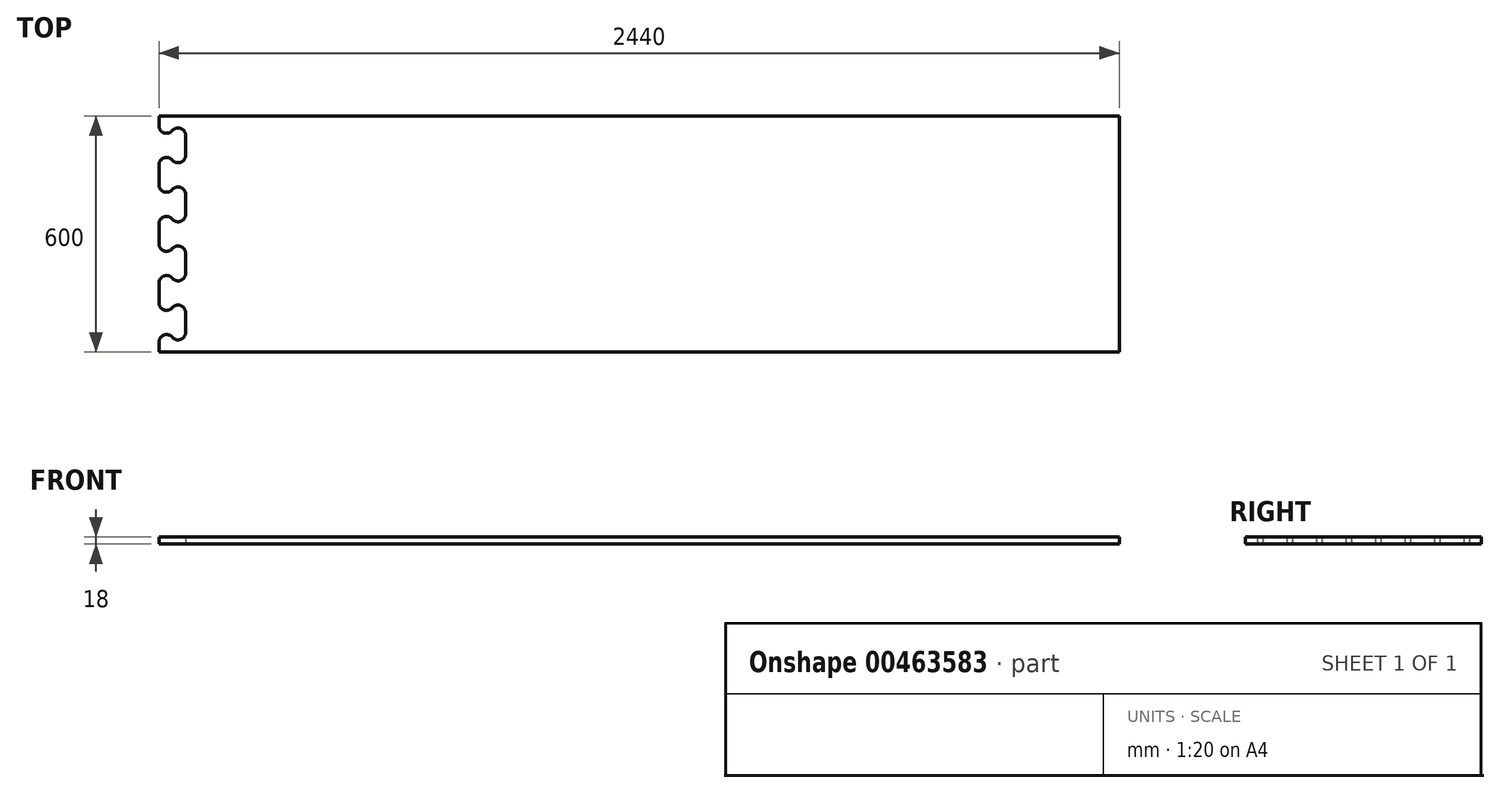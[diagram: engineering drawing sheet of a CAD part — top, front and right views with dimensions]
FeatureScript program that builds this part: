
annotation { "Feature Type Name" : "Feature", "Feature Type Description" : "" }
export const myFeature = defineFeature(function(context is Context, id is Id, definition is map)
    precondition{}
    {
        {
            var Q0;
            Q0=qCreatedBy(makeId("Top.planeOp"),FACE);
            var sketch = newSketch(context, id + "F0", { "sketchPlane" : qUnion([Q0])});
            skLineSegment(sketch, "E0.bottom", {"start": v(-1236.35, 978.6) * mm, "end": v(1203.65, 978.6) * mm});
            skLineSegment(sketch, "E0.right", {"start": v(1203.65, 978.6) * mm, "end": v(1203.65, 378.6) * mm});
            skLineSegment(sketch, "E1", {"start": v(-1236.35, 978.6) * mm, "end": v(-1236.35, 953.6) * mm});
            skLineSegment(sketch, "E2", {"start": v(-1236.35, 953.6) * mm, "end": v(-1236.35, 903.6) * mm, "construction": true});
            skLineSegment(sketch, "E3", {"start": v(-1168.41, 928.6) * mm, "end": v(-1168.41, 903.6) * mm});
            skLineSegment(sketch, "E4", {"start": v(-1236.35, 903.6) * mm, "end": v(-1168.41, 903.6) * mm, "construction": true});
            skLineSegment(sketch, "E5", {"start": v(-1236.35, 953.6) * mm, "end": v(-1168.41, 928.6) * mm, "construction": true});
            skArc(sketch, "E6", {"start": v(-1236.35, 953.6) * mm, "mid": v(-1223.73, 935.5) * mm, "end": v(-1202.38, 941.1) * mm});
            skArc(sketch, "E7", {"start": v(-1168.41, 928.6) * mm, "mid": v(-1181.04, 946.7) * mm, "end": v(-1202.38, 941.1) * mm});
            skArc(sketch, "E8.MirrorCS", {"start": v(-1236.35, 853.6) * mm, "mid": v(-1223.73, 871.7) * mm, "end": v(-1202.38, 866.1) * mm});
            skArc(sketch, "E9.MirrorCS", {"start": v(-1168.41, 878.6) * mm, "mid": v(-1181.04, 860.5) * mm, "end": v(-1202.38, 866.1) * mm});
            skLineSegment(sketch, "E10.MirrorCS", {"start": v(-1168.41, 878.6) * mm, "end": v(-1168.41, 903.6) * mm});
            skLineSegment(sketch, "E11", {"start": v(-1236.35, 853.6) * mm, "end": v(-1236.35, 803.6) * mm});
            skArc(sketch, "E12.0.1.0", {"start": v(-1236.35, 803.6) * mm, "mid": v(-1223.73, 785.5) * mm, "end": v(-1202.38, 791.1) * mm});
            skArc(sketch, "E12.0.1.1", {"start": v(-1168.41, 778.6) * mm, "mid": v(-1181.04, 796.7) * mm, "end": v(-1202.38, 791.1) * mm});
            skLineSegment(sketch, "E12.0.1.2", {"start": v(-1168.41, 778.6) * mm, "end": v(-1168.41, 753.6) * mm});
            skLineSegment(sketch, "E12.0.1.3", {"start": v(-1168.41, 728.6) * mm, "end": v(-1168.41, 753.6) * mm});
            skArc(sketch, "E12.0.1.4", {"start": v(-1168.41, 728.6) * mm, "mid": v(-1181.04, 710.5) * mm, "end": v(-1202.38, 716.1) * mm});
            skArc(sketch, "E12.0.1.5", {"start": v(-1236.35, 703.6) * mm, "mid": v(-1223.73, 721.7) * mm, "end": v(-1202.38, 716.1) * mm});
            skLineSegment(sketch, "E12.0.1.6", {"start": v(-1236.35, 703.6) * mm, "end": v(-1236.35, 653.6) * mm});
            skArc(sketch, "E12.0.2.0", {"start": v(-1236.35, 653.6) * mm, "mid": v(-1223.73, 635.5) * mm, "end": v(-1202.38, 641.1) * mm});
            skArc(sketch, "E12.0.2.1", {"start": v(-1168.41, 628.6) * mm, "mid": v(-1181.04, 646.7) * mm, "end": v(-1202.38, 641.1) * mm});
            skLineSegment(sketch, "E12.0.2.2", {"start": v(-1168.41, 628.6) * mm, "end": v(-1168.41, 603.6) * mm});
            skLineSegment(sketch, "E12.0.2.3", {"start": v(-1168.41, 578.6) * mm, "end": v(-1168.41, 603.6) * mm});
            skArc(sketch, "E12.0.2.4", {"start": v(-1168.41, 578.6) * mm, "mid": v(-1181.04, 560.5) * mm, "end": v(-1202.38, 566.1) * mm});
            skArc(sketch, "E12.0.2.5", {"start": v(-1236.35, 553.6) * mm, "mid": v(-1223.73, 571.7) * mm, "end": v(-1202.38, 566.1) * mm});
            skLineSegment(sketch, "E12.0.2.6", {"start": v(-1236.35, 553.6) * mm, "end": v(-1236.35, 503.6) * mm});
            skArc(sketch, "E12.0.3.0", {"start": v(-1236.35, 503.6) * mm, "mid": v(-1223.73, 485.5) * mm, "end": v(-1202.38, 491.1) * mm});
            skArc(sketch, "E12.0.3.1", {"start": v(-1168.41, 478.6) * mm, "mid": v(-1181.04, 496.7) * mm, "end": v(-1202.38, 491.1) * mm});
            skLineSegment(sketch, "E12.0.3.2", {"start": v(-1168.41, 478.6) * mm, "end": v(-1168.41, 453.6) * mm});
            skLineSegment(sketch, "E12.0.3.3", {"start": v(-1168.41, 428.6) * mm, "end": v(-1168.41, 453.6) * mm});
            skArc(sketch, "E12.0.3.4", {"start": v(-1168.41, 428.6) * mm, "mid": v(-1181.04, 410.5) * mm, "end": v(-1202.38, 416.1) * mm});
            skArc(sketch, "E12.0.3.5", {"start": v(-1236.35, 403.6) * mm, "mid": v(-1223.73, 421.7) * mm, "end": v(-1202.38, 416.1) * mm});
            skLineSegment(sketch, "E12.0.3.6", {"start": v(-1236.35, 403.6) * mm, "end": v(-1236.35, 378.6) * mm});
            skLineSegment(sketch, "E12.direction1", {"start": v(-1236.35, 803.6) * mm, "end": v(-1211.35, 803.6) * mm, "construction": true});
            skLineSegment(sketch, "E12.direction2", {"start": v(-1236.35, 803.6) * mm, "end": v(-1236.35, 653.6) * mm, "construction": true});
            skLineSegment(sketch, "E13.0", {"start": v(-1236.35, 378.6) * mm, "end": v(1203.65, 378.6) * mm});
            skSolve(sketch);
        }
        {
            var Q0;
            Q0=makeQuery(id+"F0.imprint","IMPRINT",FACE,{"disambiguationData":[TD([[makeQuery(id+"F0.imprint","IMPRINT",EDGE,{"derivedFrom":sQuery(id+"F0.wireOp",EDGE,"E0.bottom")}),-1.0]])]});
            extrude(context, id + "F1", {"entities" : qUnion([Q0]), "depth" : 18 * mm});
        }
    });
